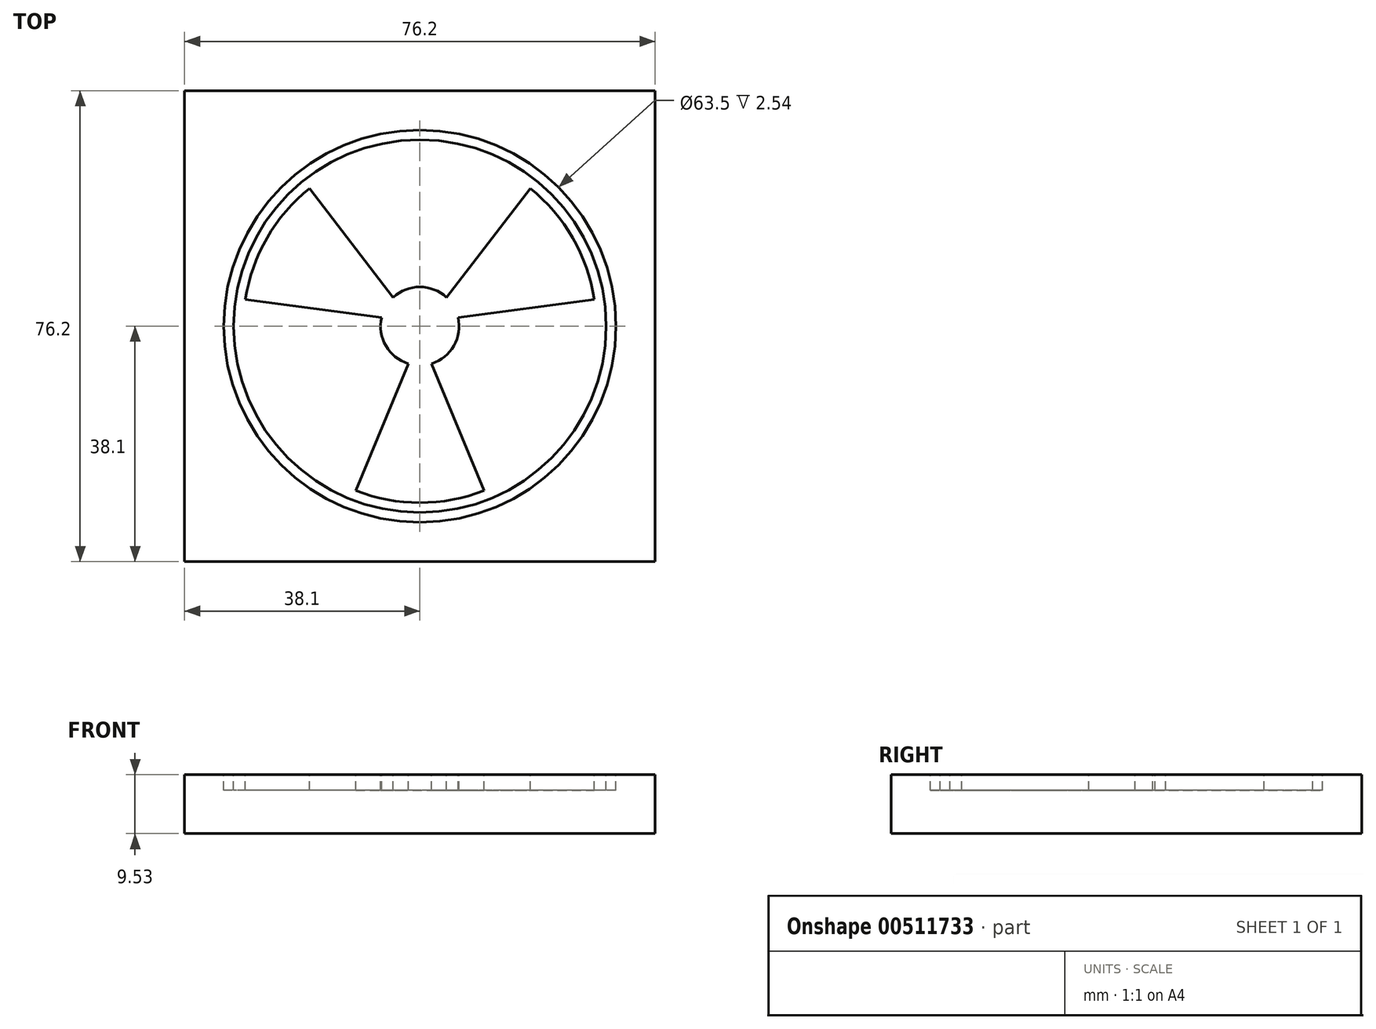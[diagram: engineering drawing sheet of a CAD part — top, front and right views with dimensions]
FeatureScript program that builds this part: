
annotation { "Feature Type Name" : "Feature", "Feature Type Description" : "" }
export const myFeature = defineFeature(function(context is Context, id is Id, definition is map)
    precondition{}
    {
        {
            var Q0;
            Q0=qCreatedBy(makeId("Top.planeOp"),FACE);
            var sketch = newSketch(context, id + "F0", { "sketchPlane" : qUnion([Q0])});
            skLineSegment(sketch, "E0.bottom", {"start": v(38.1, 38.1) * mm, "end": v(-38.1, 38.1) * mm});
            skLineSegment(sketch, "E0.top", {"start": v(38.1, -38.1) * mm, "end": v(-38.1, -38.1) * mm});
            skLineSegment(sketch, "E0.left", {"start": v(38.1, 38.1) * mm, "end": v(38.1, -38.1) * mm});
            skLineSegment(sketch, "E0.right", {"start": v(-38.1, 38.1) * mm, "end": v(-38.1, -38.1) * mm});
            skPoint(sketch, "E0.middle", {"position": v(0, 0) * mm});
            skSolve(sketch);
        }
        {
            var Q0;
            Q0 = qSketchRegion(id + "F0", true);
            extrude(context, id + "F1", {"entities" : qUnion([Q0]), "depth" : 9.52 * mm});
        }
        {
            var Q0;
            Q0=makeQuery(id+"F1.opExtrude","CAP_FACE",FACE,{"disambiguationData":[OSD([sQuery(id+"F0.wireOp",EDGE,"E0.bottom"),sQuery(id+"F0.wireOp",EDGE,"E0.top"),sQuery(id+"F0.wireOp",EDGE,"E0.left"),sQuery(id+"F0.wireOp",EDGE,"E0.right")])],"isStart":false});
            var sketch = newSketch(context, id + "F2", { "sketchPlane" : qUnion([Q0])});
            skCircle(sketch, "E1", {"center": v(0, 0) * mm, "radius": 31.75 * mm});
            skCircle(sketch, "E2", {"center": v(0, 0) * mm, "radius": 30.16 * mm});
            skArc(sketch, "E3", {"start": v(-6.2, 1.41) * mm, "mid": v(-5.5, -3.17) * mm, "end": v(-1.87, -6.07) * mm});
            skLineSegment(sketch, "E4", {"start": v(-4.32, 4.66) * mm, "end": v(-18.83, 23.56) * mm});
            skLineSegment(sketch, "E5", {"start": v(4.32, 4.66) * mm, "end": v(18.83, 23.56) * mm});
            skLineSegment(sketch, "E6", {"start": v(-18.83, 23.56) * mm, "end": v(0, 6.35) * mm, "construction": true});
            skLineSegment(sketch, "E7", {"start": v(0, 6.35) * mm, "end": v(18.83, 23.56) * mm, "construction": true});
            skLineSegment(sketch, "E8", {"start": v(-4.32, 4.66) * mm, "end": v(4.32, 4.66) * mm, "construction": true});
            skLineSegment(sketch, "E9.1.0", {"start": v(-1.87, -6.07) * mm, "end": v(-11, -28.09) * mm});
            skLineSegment(sketch, "E9.1.1", {"start": v(-6.2, 1.41) * mm, "end": v(-29.82, 4.52) * mm});
            skLineSegment(sketch, "E9.2.0", {"start": v(6.2, 1.41) * mm, "end": v(29.82, 4.52) * mm});
            skLineSegment(sketch, "E9.2.1", {"start": v(1.87, -6.07) * mm, "end": v(11, -28.09) * mm});
            skArc(sketch, "E10.trimOffspring", {"start": v(1.87, -6.07) * mm, "mid": v(5.5, -3.18) * mm, "end": v(6.2, 1.41) * mm});
            skArc(sketch, "E11.trimOffspring", {"start": v(4.32, 4.66) * mm, "mid": v(0, 6.35) * mm, "end": v(-4.32, 4.66) * mm});
            skArc(sketch, "E12", {"start": v(-17.64, 22.48) * mm, "mid": v(-24.68, 14.4) * mm, "end": v(-28.25, 4.32) * mm});
            skArc(sketch, "E13.trimOffspring", {"start": v(-10.39, -26.62) * mm, "mid": v(0, -28.58) * mm, "end": v(10.39, -26.62) * mm});
            skArc(sketch, "E14.trimOffspring", {"start": v(28.25, 4.32) * mm, "mid": v(24.68, 14.4) * mm, "end": v(17.64, 22.48) * mm});
            skSolve(sketch);
        }
        {
            var Q0;
            Q0 = qSketchRegion(id + "F2", true);
            var Q1;
            Q1=makeQuery(id+"F2.imprint","IMPRINT",FACE,{"disambiguationData":[TD([[makeQuery(id+"F2.imprint","IMPRINT",EDGE,{"derivedFrom":sQuery(id+"F2.wireOp",EDGE,"E3")}),1.0]])]});
            extrude(context, id + "F3", {"entities" : qUnion([Q0, Q1]), "operationType" : NewBodyOperationType.REMOVE, "oppositeDirection" : true, "depth" : 2.54 * mm});
        }
    });
